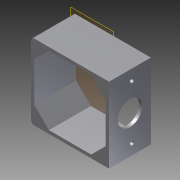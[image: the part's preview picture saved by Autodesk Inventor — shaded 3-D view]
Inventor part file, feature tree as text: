
AUTODESK INVENTOR PART (.ipt)
format: ipt  version: 2012 (Build 160160000, 160)  size: 121,344 bytes
history: native  units: in
note: dims shown in document units (in); Inventor stores cm internally (conversion verified against a paired STEP export)
features: reference x6, extrude x4, sketch x4, plane x2
ambient origin geometry x8: Origin, YZ Plane, XZ Plane, XY Plane, X Axis, Y Axis, Z Axis, Center Point
feature tree (16):
  plane  "Work Plane1"
  extrude  "Extrusion2"  Depth=0.5906in
  extrude  "Extrusion3"  Depth=1.0138in TaperAngle=0.0deg
  sketch  "Sketch7"  dims[d15=1.0138in d16=0.0in]
  plane  "Work Plane2"
  extrude  "Extrusion5"  [1 undecoded]
  extrude  "Extrusion6"  [1 undecoded]
  sketch  "Sketch3"  dims[d2=1.0138in d3=0.0in d4=0.5906in]
  reference  "Reference3"
  reference  "Reference4"
  sketch  "Sketch5"  dims[d5=1.0138in d6=0.0in d13=1.0138in d14=0.0in]
  reference  "Reference5"
  reference  "Reference6"
  sketch  "Sketch8"
  reference  "Reference7"
  reference  "Reference8"
note: 2 required parameter values undecoded (feature->parameter linkage not recoverable at this tier; creation-order binding heuristic only, values carry confidence <= 0.55)
